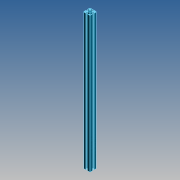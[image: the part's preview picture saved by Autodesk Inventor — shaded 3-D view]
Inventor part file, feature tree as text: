
AUTODESK INVENTOR PART (.ipt)
format: ipt  version: 2019 (Build 230136000, 136)  size: 416,768 bytes
history: native  units: mm
features: fillet x8, sketch x4, extrude x3, projected_geometry x2, mirror x1, pattern_circular x1, hole x1
ambient origin geometry x8: Origin, YZ Plane, XZ Plane, XY Plane, X Axis, Y Axis, Z Axis, Center Point
bodies: Solid1 (feature_tree)
feature tree (20):
  extrude  "Corps"  TaperAngle=45.0deg  [1 undecoded]
  extrude  "Creux"  Depth=1.5mm
  fillet  "Fillet8"  Radius=4.0mm
  fillet  "Fillet1"  Radius=2.0mm
  fillet  "Fillet2"  Radius=4.3mm
  fillet  "Fillet3"  Radius=2.0mm
  fillet  "Fillet4"  Radius=10.0mm
  fillet  "Fillet5"  Radius=6.5mm
  mirror  "Mirror1"
  fillet  "Fillet6"  Radius=7.5mm
  fillet  "Fillet7"  Radius=300.0mm
  pattern_circular  "Circular Pattern1"  [2 undecoded]
  hole  "Hole1"  [1 undecoded]
  extrude  "Extrusion4"  Depth=0.5mm
  sketch  "Sketch1"  dims[d0=20.0mm d1=45.0deg]
  sketch  "Sketch2"  dims[d2=800.0mm d3=0.0mm d4=1.5mm d5=4.0mm d6=2.0mm d7=4.3mm d8=2.0mm d9=10.0mm d10=6.5mm d12=7.5mm d13=300.0mm d14=0.0mm]
  sketch  "Sketch3"  dims[d15=3.0mm]
  sketch  "Sketch4"  dims[d16=1.0mm d17=2.0mm d18=0.5mm d19=0.5mm d20=3.0mm d21=1.0mm d22=40.0mm d23=360.0deg d25=6.0mm d26=6.0mm d27=4.0mm d28=2.0mm d29=90.0deg d30=8.0mm d31=20.594885mm d32=1.0mm d35=800.0mm d36=0.0mm]
  projected_geometry  "Project Cut Edges1"
  projected_geometry  "Project Cut Edges2"
note: 4 required parameter values undecoded (feature->parameter linkage not recoverable at this tier; creation-order binding heuristic only, values carry confidence <= 0.55)
